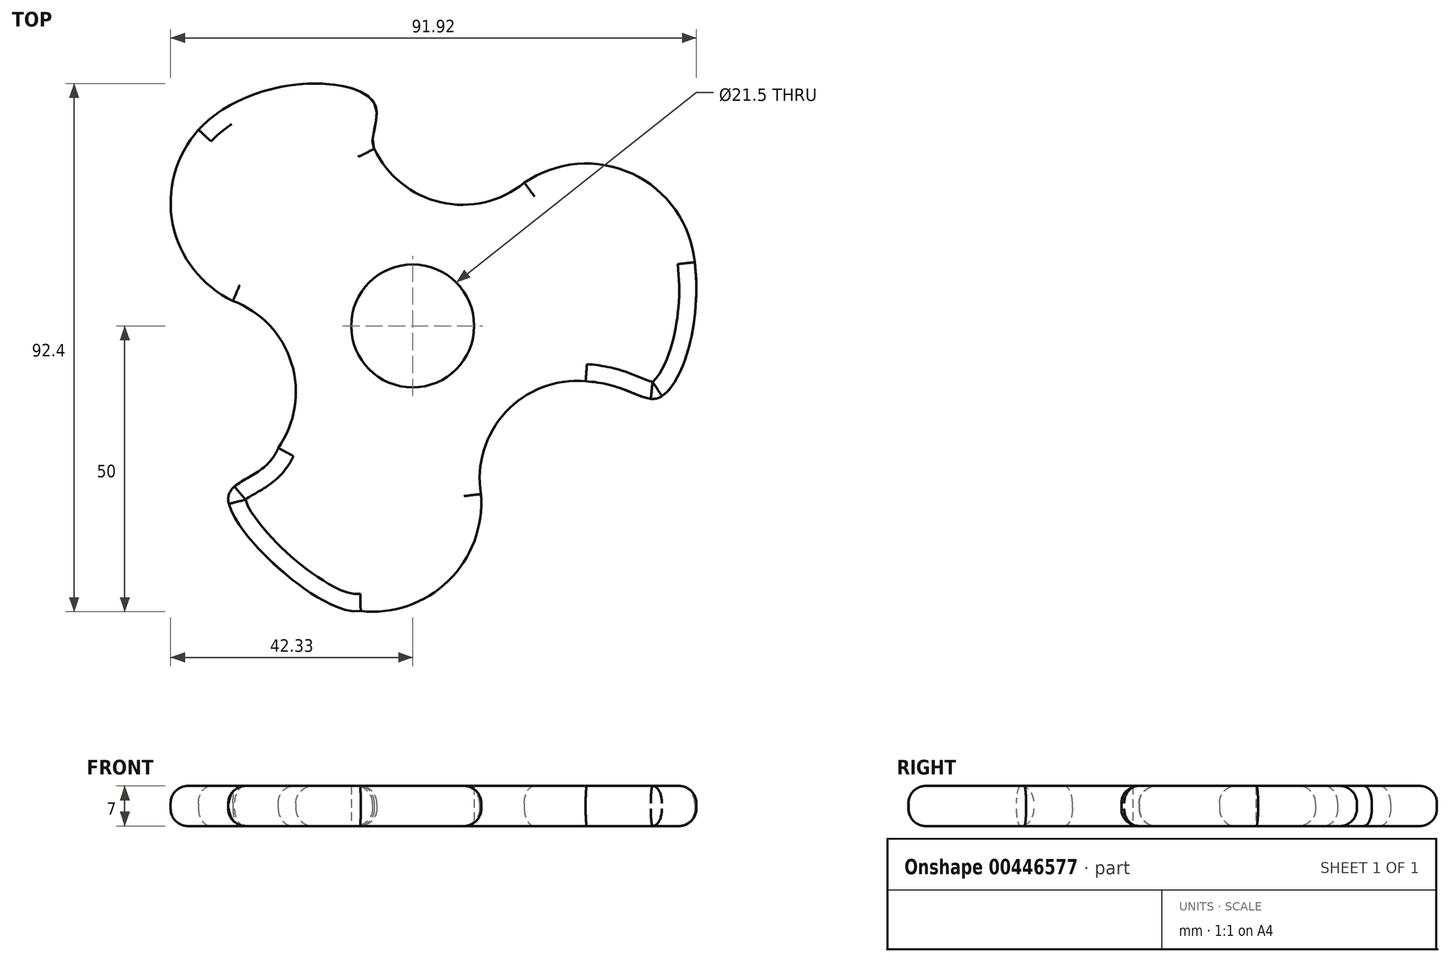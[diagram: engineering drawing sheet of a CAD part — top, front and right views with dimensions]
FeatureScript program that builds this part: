
annotation { "Feature Type Name" : "Feature", "Feature Type Description" : "" }
export const myFeature = defineFeature(function(context is Context, id is Id, definition is map)
    precondition{}
    {
        {
            var Q0;
            Q0=qCreatedBy(makeId("Top.planeOp"),FACE);
            var sketch = newSketch(context, id + "F0", { "sketchPlane" : qUnion([Q0])});
            skCircle(sketch, "E0", {"center": v(0, 0) * mm, "radius": 31.75 * mm});
            skCircle(sketch, "E1", {"center": v(30.34, 9.36) * mm, "radius": 19.05 * mm});
            skCircle(sketch, "E2", {"center": v(-23.28, 21.6) * mm, "radius": 19.05 * mm});
            skCircle(sketch, "E3", {"center": v(-7.07, -30.95) * mm, "radius": 19.05 * mm});
            skArc(sketch, "E4", {"start": v(-6.73, 31.03) * mm, "mid": v(4.93, 21.62) * mm, "end": v(19.52, 25.04) * mm});
            skArc(sketch, "E5", {"start": v(30.24, -9.69) * mm, "mid": v(16.25, -15.08) * mm, "end": v(11.92, -29.43) * mm});
            skArc(sketch, "E6", {"start": v(-23.51, -21.34) * mm, "mid": v(-21.19, -6.54) * mm, "end": v(-31.45, 4.38) * mm});
            skCircle(sketch, "E7", {"center": v(0, 0) * mm, "radius": 10.75 * mm});
            skFitSpline(sketch, "E8", {"points": [v(-9.1, -49.9) * mm, v(-32.25, -30.32) * mm, v(-23.51, -21.34) * mm], "startDerivative": vector(-34, -5.1) * mm, "endDerivative": vector(17.72, 43.04) * mm});
            skFitSpline(sketch, "E9", {"points": [v(-37.46, 34.31) * mm, v(-6.73, 39) * mm, v(-6.73, 31.03) * mm], "startDerivative": vector(42, 45.44) * mm, "endDerivative": vector(10.34, -15.99) * mm});
            skFitSpline(sketch, "E10", {"points": [v(49.3, 11.14) * mm, v(43.2, -12.5) * mm, v(30.24, -9.69) * mm], "startDerivative": vector(7.14, -58.04) * mm, "endDerivative": vector(-53.47, 3.26) * mm});
            skSolve(sketch);
        }
        {
            var Q0;
            {var subQ0=sQuery(id+"F0.wireOp",EDGE,"E4");var subQ1=sQuery(id+"F0.wireOp",EDGE,"E1");var subQ6=makeQuery(id+"F0.imprint","INTERSECT",VERTEX,{"derivedFrom":[subQ1,subQ0]});Q0=makeQuery(id+"F0.imprint","IMPRINT",FACE,{"disambiguationData":[TD([[makeQuery(id+"F0.imprint","IMPRINT",EDGE,{"disambiguationData":[TD([[subQ6,-1.0]])],"derivedFrom":subQ1}),1.0]])]});}
            var Q1;
            {var subQ0=sQuery(id+"F0.wireOp",EDGE,"E1");var subQ1=sQuery(id+"F0.wireOp",EDGE,"E0");var subQ2=makeQuery(id+"F0.imprint","INTERSECT",VERTEX,{"derivedFrom":[subQ1,subQ0,sQuery(id+"F0.wireOp",EDGE,"E4")]});Q1=makeQuery(id+"F0.imprint","IMPRINT",FACE,{"disambiguationData":[TD([[makeQuery(id+"F0.imprint","IMPRINT",EDGE,{"disambiguationData":[TD([[subQ2,1.0]])],"derivedFrom":subQ1}),-1.0]])]});}
            var Q2;
            {var subQ0=sQuery(id+"F0.wireOp",EDGE,"E4");var subQ1=sQuery(id+"F0.wireOp",EDGE,"E1");var subQ2=makeQuery(id+"F0.imprint","INTERSECT",VERTEX,{"derivedFrom":[subQ1,subQ0]});Q2=makeQuery(id+"F0.imprint","IMPRINT",FACE,{"disambiguationData":[TD([[makeQuery(id+"F0.imprint","IMPRINT",EDGE,{"disambiguationData":[TD([[subQ2,-1.0]])],"derivedFrom":subQ1}),-1.0]])]});}
            var Q3;
            {var subQ0=sQuery(id+"F0.wireOp",EDGE,"E3");var subQ1=sQuery(id+"F0.wireOp",EDGE,"E0");var subQ2=makeQuery(id+"F0.imprint","INTERSECT",VERTEX,{"derivedFrom":[subQ1,subQ0,sQuery(id+"F0.wireOp",EDGE,"E5")]});Q3=makeQuery(id+"F0.imprint","IMPRINT",FACE,{"disambiguationData":[TD([[makeQuery(id+"F0.imprint","IMPRINT",EDGE,{"disambiguationData":[TD([[subQ2,1.0]])],"derivedFrom":subQ1}),-1.0]])]});}
            var Q4;
            {var subQ0=sQuery(id+"F0.wireOp",EDGE,"E5");var subQ1=sQuery(id+"F0.wireOp",EDGE,"E3");var subQ6=makeQuery(id+"F0.imprint","INTERSECT",VERTEX,{"derivedFrom":[subQ1,subQ0]});Q4=makeQuery(id+"F0.imprint","IMPRINT",FACE,{"disambiguationData":[TD([[makeQuery(id+"F0.imprint","IMPRINT",EDGE,{"disambiguationData":[TD([[subQ6,-1.0]])],"derivedFrom":subQ1}),1.0]])]});}
            var Q5;
            {var subQ0=sQuery(id+"F0.wireOp",EDGE,"E4");var subQ1=sQuery(id+"F0.wireOp",EDGE,"E2");var subQ7=makeQuery(id+"F0.imprint","INTERSECT",VERTEX,{"derivedFrom":[subQ1,subQ0]});Q5=makeQuery(id+"F0.imprint","IMPRINT",FACE,{"disambiguationData":[TD([[makeQuery(id+"F0.imprint","IMPRINT",EDGE,{"disambiguationData":[TD([[subQ7,1.0]])],"derivedFrom":subQ1}),1.0]])]});}
            var Q6;
            {var subQ0=sQuery(id+"F0.wireOp",EDGE,"E2");var subQ1=sQuery(id+"F0.wireOp",EDGE,"E0");var subQ2=makeQuery(id+"F0.imprint","INTERSECT",VERTEX,{"derivedFrom":[subQ1,subQ0,sQuery(id+"F0.wireOp",EDGE,"E4")]});Q6=makeQuery(id+"F0.imprint","IMPRINT",FACE,{"disambiguationData":[TD([[makeQuery(id+"F0.imprint","IMPRINT",EDGE,{"disambiguationData":[TD([[subQ2,-1.0]])],"derivedFrom":subQ1}),-1.0]])]});}
            var Q7;
            {var subQ0=sQuery(id+"F0.wireOp",EDGE,"E9");var subQ1=sQuery(id+"F0.wireOp",EDGE,"E2");var subQ2=makeQuery(id+"F0.imprint","INTERSECT",VERTEX,{"disambiguationData":[OD(1.0)],"derivedFrom":[subQ1,subQ0]});Q7=makeQuery(id+"F0.imprint","IMPRINT",FACE,{"disambiguationData":[TD([[makeQuery(id+"F0.imprint","IMPRINT",EDGE,{"disambiguationData":[TD([[subQ2,-1.0]])],"derivedFrom":subQ1}),-1.0]])]});}
            var Q8;
            {var subQ0=sQuery(id+"F0.wireOp",EDGE,"E10");Q8=makeQuery(id+"F0.imprint","IMPRINT",FACE,{"disambiguationData":[TD([[makeQuery(id+"F0.imprint","IMPRINT",EDGE,{"derivedFrom":subQ0}),-1.0]])]});}
            var Q9;
            {var subQ0=sQuery(id+"F0.wireOp",EDGE,"E8");var subQ1=sQuery(id+"F0.wireOp",EDGE,"E3");var subQ2=makeQuery(id+"F0.imprint","INTERSECT",VERTEX,{"disambiguationData":[OD(0.0)],"derivedFrom":[subQ1,subQ0]});Q9=makeQuery(id+"F0.imprint","IMPRINT",FACE,{"disambiguationData":[TD([[makeQuery(id+"F0.imprint","IMPRINT",EDGE,{"disambiguationData":[TD([[subQ2,1.0]])],"derivedFrom":subQ1}),-1.0]])]});}
            extrude(context, id + "F1", {"entities" : qUnion([Q0, Q1, Q2, Q3, Q4, Q5, Q6, Q7, Q8, Q9]), "endBound" : BoundingType.SYMMETRIC, "depth" : 7 * mm});
        }
        {
            var Q0;
            Q0=makeQuery(id+"F1.opExtrude","CAP_EDGE",EDGE,{"disambiguationData":[OSD([sQuery(id+"F0.wireOp",EDGE,"E10")])],"isStart":true});
            var Q1;
            Q1=makeQuery(id+"F1.opExtrude","CAP_EDGE",EDGE,{"disambiguationData":[OSD([sQuery(id+"F0.wireOp",EDGE,"E1")])],"isStart":true});
            var Q2;
            Q2=makeQuery(id+"F1.opExtrude","CAP_EDGE",EDGE,{"disambiguationData":[OSD([sQuery(id+"F0.wireOp",EDGE,"E4")])],"isStart":true});
            var Q3;
            Q3=makeQuery(id+"F1.opExtrude","CAP_EDGE",EDGE,{"disambiguationData":[OSD([sQuery(id+"F0.wireOp",EDGE,"E9")])],"isStart":true});
            var Q4;
            Q4=makeQuery(id+"F1.opExtrude","CAP_EDGE",EDGE,{"disambiguationData":[OSD([sQuery(id+"F0.wireOp",EDGE,"E2")])],"isStart":true});
            var Q5;
            Q5=makeQuery(id+"F1.opExtrude","CAP_EDGE",EDGE,{"disambiguationData":[OSD([sQuery(id+"F0.wireOp",EDGE,"E6")])],"isStart":true});
            var Q6;
            Q6=makeQuery(id+"F1.opExtrude","CAP_EDGE",EDGE,{"disambiguationData":[OSD([sQuery(id+"F0.wireOp",EDGE,"E8")])],"isStart":true});
            var Q7;
            Q7=makeQuery(id+"F1.opExtrude","CAP_EDGE",EDGE,{"disambiguationData":[OSD([sQuery(id+"F0.wireOp",EDGE,"E3")])],"isStart":true});
            var Q8;
            Q8=makeQuery(id+"F1.opExtrude","CAP_EDGE",EDGE,{"disambiguationData":[OSD([sQuery(id+"F0.wireOp",EDGE,"E5")])],"isStart":true});
            fillet(context, id + "F2", {"entities" : qUnion([Q0, Q1, Q2, Q3, Q4, Q5, Q6, Q7, Q8]), "radius" : 3 * mm, "tangentPropagation" : true, "allowEdgeOverflow" : false});
        }
        {
            var Q0;
            Q0=makeQuery(id+"F1.opExtrude","CAP_EDGE",EDGE,{"disambiguationData":[OSD([sQuery(id+"F0.wireOp",EDGE,"E10")])],"isStart":false});
            var Q1;
            Q1=makeQuery(id+"F1.opExtrude","CAP_EDGE",EDGE,{"disambiguationData":[OSD([sQuery(id+"F0.wireOp",EDGE,"E5")])],"isStart":false});
            var Q2;
            Q2=makeQuery(id+"F1.opExtrude","CAP_EDGE",EDGE,{"disambiguationData":[OSD([sQuery(id+"F0.wireOp",EDGE,"E3")])],"isStart":false});
            var Q3;
            Q3=makeQuery(id+"F1.opExtrude","CAP_EDGE",EDGE,{"disambiguationData":[OSD([sQuery(id+"F0.wireOp",EDGE,"E8")])],"isStart":false});
            var Q4;
            Q4=makeQuery(id+"F1.opExtrude","CAP_EDGE",EDGE,{"disambiguationData":[OSD([sQuery(id+"F0.wireOp",EDGE,"E6")])],"isStart":false});
            var Q5;
            Q5=makeQuery(id+"F1.opExtrude","CAP_EDGE",EDGE,{"disambiguationData":[OSD([sQuery(id+"F0.wireOp",EDGE,"E1")])],"isStart":false});
            var Q6;
            Q6=makeQuery(id+"F1.opExtrude","CAP_EDGE",EDGE,{"disambiguationData":[OSD([sQuery(id+"F0.wireOp",EDGE,"E4")])],"isStart":false});
            var Q7;
            Q7=makeQuery(id+"F1.opExtrude","CAP_EDGE",EDGE,{"disambiguationData":[OSD([sQuery(id+"F0.wireOp",EDGE,"E9")])],"isStart":false});
            var Q8;
            Q8=makeQuery(id+"F1.opExtrude","CAP_EDGE",EDGE,{"disambiguationData":[OSD([sQuery(id+"F0.wireOp",EDGE,"E2")])],"isStart":false});
            fillet(context, id + "F3", {"entities" : qUnion([Q0, Q1, Q2, Q3, Q4, Q5, Q6, Q7, Q8]), "radius" : 3 * mm, "tangentPropagation" : true, "allowEdgeOverflow" : false});
        }
    });
